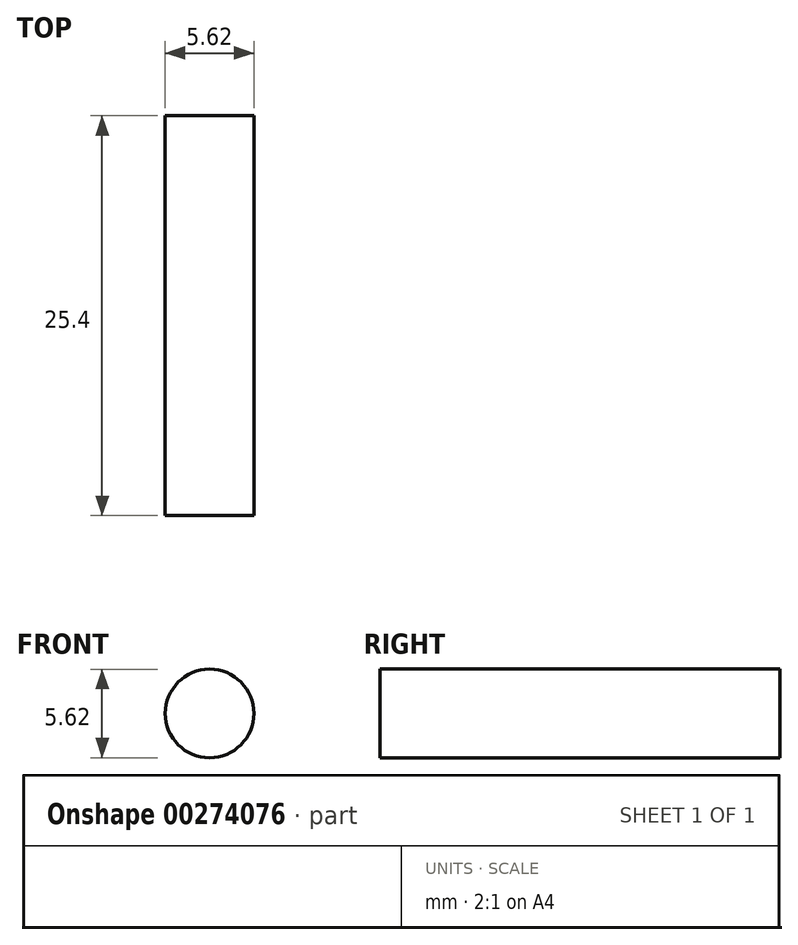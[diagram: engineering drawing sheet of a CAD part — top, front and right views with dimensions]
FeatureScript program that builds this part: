
annotation { "Feature Type Name" : "Feature", "Feature Type Description" : "" }
export const myFeature = defineFeature(function(context is Context, id is Id, definition is map)
    precondition{}
    {
        {
            var Q0;
            Q0=qCreatedBy(makeId("Front.planeOp"),FACE);
            var sketch = newSketch(context, id + "F0", { "sketchPlane" : qUnion([Q0])});
            skCircle(sketch, "E0", {"center": v(0, 0) * mm, "radius": 2.81 * mm});
            skSolve(sketch);
        }
        {
            var Q0;
            Q0 = qSketchRegion(id + "F0", true);
            extrude(context, id + "F1", {"entities" : qUnion([Q0]), "depth" : 25.4 * mm});
        }
    });
